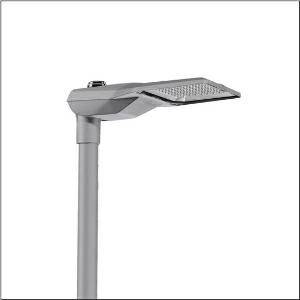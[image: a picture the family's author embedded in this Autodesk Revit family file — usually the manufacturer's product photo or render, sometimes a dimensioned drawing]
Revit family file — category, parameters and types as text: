
# Revit family: streetlight_sl_21_midi___st0_5a_5xe7b37n08mb_20a0
name_source: partatom
category: Lighting Fixtures
units: mm (PartAtom-declared; Revit-internal decimal feet)

## family parameters
Cut with Voids When Loaded = No
Host = Face
Light Source = No
Part Type = Normal
Room Calculation Point = No
Round Connector Dimension = Use Diameter
Shared = No

## types (1)
- --- (1 x LED, 18270 lm, 136 W, 3000K)
    Apparent Load = 136 VA
    CIE Flux Codes = 41 75 97 100 100
    Color Rendering = 70
    Color Temperature = 3000K
    Default Elevation = 1800 mm
    Description = Streetlight SL 21 midi, mast luminaire, primary light control with lens, of PMMA, primary optical cover: cover, of toughened safety glass, transparent, light distribution: ST0.5a, light emission: direct distribution, primary light characteristic: asymmetric, installation type: side-entry, LED, 3G 2.5mm², High Power LED, rated luminous flux: 18.270lm, luminous efficacy: 134lm/W, light colour: 730, colour temperature: 3000K, control gear: NEMA (7pin), control: overheat protection, pre-setting: linear dimming characteristic, constant luminous flux control, time-dependent luminous flux control, flexible luminous flux parameterisation, mains connection: 220..240V, AC, 50/60Hz, connection cable pre-assembled, cable length: 12,5m, wiring characteristics: H05VV-F, start of lifetime: 136W, end of service life: 142W, reduction: 61W, luminaire housing, of diecast aluminium (EN AC-44300), powder-coated, Siteco® metallic grey (DB 702S), corrosivity category C5 mid according to DIN EN ISO 12944, multi-level sealing system, sealing non-destructively replaceable, inclination adjustable: 0°, 5°, 10°, 15°, length: 644mm, width: 335mm, height: 110mm, spigot size: 42mm (side-entry), mounting height: 4..8m, protection rating (complete): IP66, insulation class (complete): insulation class I (protective earthing), certification: CE, ENEC, ENEC+, VDE, impact resistance: IK09, permissible operating ambient temperature for outdoor applications: -40..+50°C, standard-compliant lighting for roads and squares, packaging unit: 1 piece

Light Distribution: ST0.5a
    Height = 111 mm
    Lamp = 1 x LED
    Lamp Light Flux = 18270 lm
    Lamp Power = 136 W
    Lamp count = 1
    Length = 644 mm
    Luminous efficacy = 134 lm/W
    Manufacturer = Siteco
    ModVariant = No
    Model = 5XE7B37N08MB
    Number of Poles = 1
    OnlyDefault = Yes
    Power Factor = 1
    Product Name = Streetlight SL 21 midi | ST0.5a
    Product group = mast luminaire | pylon top
    ProductGroupID = 6100
    Protection Class = Protection class I
    Protection Degree = IP 66
    RLX_Detail_Level = 1
    RLX_Emergency_Light_Flux = 0 lm
    RLX_Emergency_Type = 0
    RLX_Emergency_Type_DB = No
    RlxData = <blob elided: 101301 chars, md5=ab91aa80>
    Socket = socket
    Standby Power = 0 W
    System Light Flux = 18270 lm
    System Power = 136 W
    Type Comments = factory setting: luminous flux: 100 % | dim-lin: 254 | 695 mA
    Type Image = l_1294377.jpg
    URL = http://relux.com
    VarID = @adj_132646
    Voltage = 0 V
    Weight = 0.00 kg
    Width = 336 mm

## geometry (parser evidence)
native form markers: Blend x4, Sweep x12
no freeform markers — native parametric forms only
